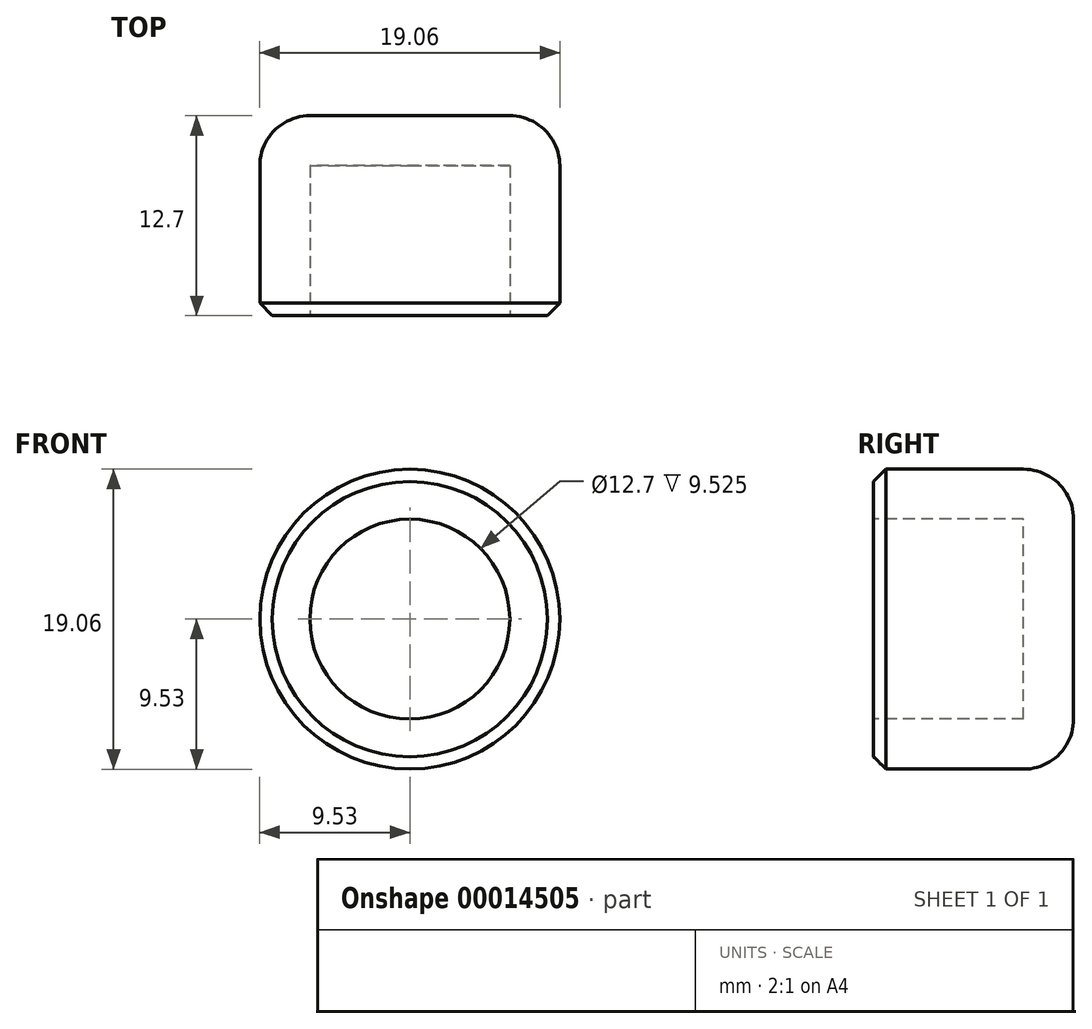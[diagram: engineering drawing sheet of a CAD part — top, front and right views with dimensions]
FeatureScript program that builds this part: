
annotation { "Feature Type Name" : "Feature", "Feature Type Description" : "" }
export const myFeature = defineFeature(function(context is Context, id is Id, definition is map)
    precondition{}
    {
        {
            var Q0;
            Q0=qCreatedBy(makeId("Front.planeOp"),FACE);
            var sketch = newSketch(context, id + "F0", { "sketchPlane" : qUnion([Q0])});
            skCircle(sketch, "E0", {"center": v(0, 0) * mm, "radius": 9.53 * mm});
            skSolve(sketch);
        }
        {
            var Q0;
            Q0 = qSketchRegion(id + "F0", true);
            extrude(context, id + "F1", {"entities" : qUnion([Q0]), "depth" : 12.7 * mm});
        }
        {
            var Q0;
            Q0=makeQuery(id+"F1.opExtrude","CAP_FACE",FACE,{"disambiguationData":[OSD([sQuery(id+"F0.wireOp",EDGE,"E0")])],"isStart":false});
            var sketch = newSketch(context, id + "F2", { "sketchPlane" : qUnion([Q0])});
            skCircle(sketch, "E1", {"center": v(0, 0) * mm, "radius": 6.35 * mm});
            skSolve(sketch);
        }
        {
            var Q0;
            Q0=makeQuery(id+"F2.imprint","IMPRINT",FACE,{"disambiguationData":[TD([[makeQuery(id+"F2.imprint","IMPRINT",EDGE,{"derivedFrom":sQuery(id+"F2.wireOp",EDGE,"E1")}),1.0]])]});
            extrude(context, id + "F3", {"entities" : qUnion([Q0]), "operationType" : NewBodyOperationType.REMOVE, "oppositeDirection" : true, "depth" : 9.52 * mm});
        }
        {
            var Q0;
            Q0=makeQuery(id+"F1.opExtrude","CAP_EDGE",EDGE,{"disambiguationData":[OSD([sQuery(id+"F0.wireOp",EDGE,"E0")])],"isStart":true});
            fillet(context, id + "F4", {"entities" : qUnion([Q0]), "radius" : 3.17 * mm, "tangentPropagation" : true, "allowEdgeOverflow" : false});
        }
        {
            var Q0;
            Q0=makeQuery(id+"F1.opExtrude","CAP_EDGE",EDGE,{"disambiguationData":[OSD([sQuery(id+"F0.wireOp",EDGE,"E0")])],"isStart":false});
            chamfer(context, id + "F5", {"entities" : qUnion([Q0]), "chamferType" : ChamferType.OFFSET_ANGLE, "width" : 0.79 * mm, "oppositeDirection" : false, "angle" : 45 * degree, "tangentPropagation" : true});
        }
    });
